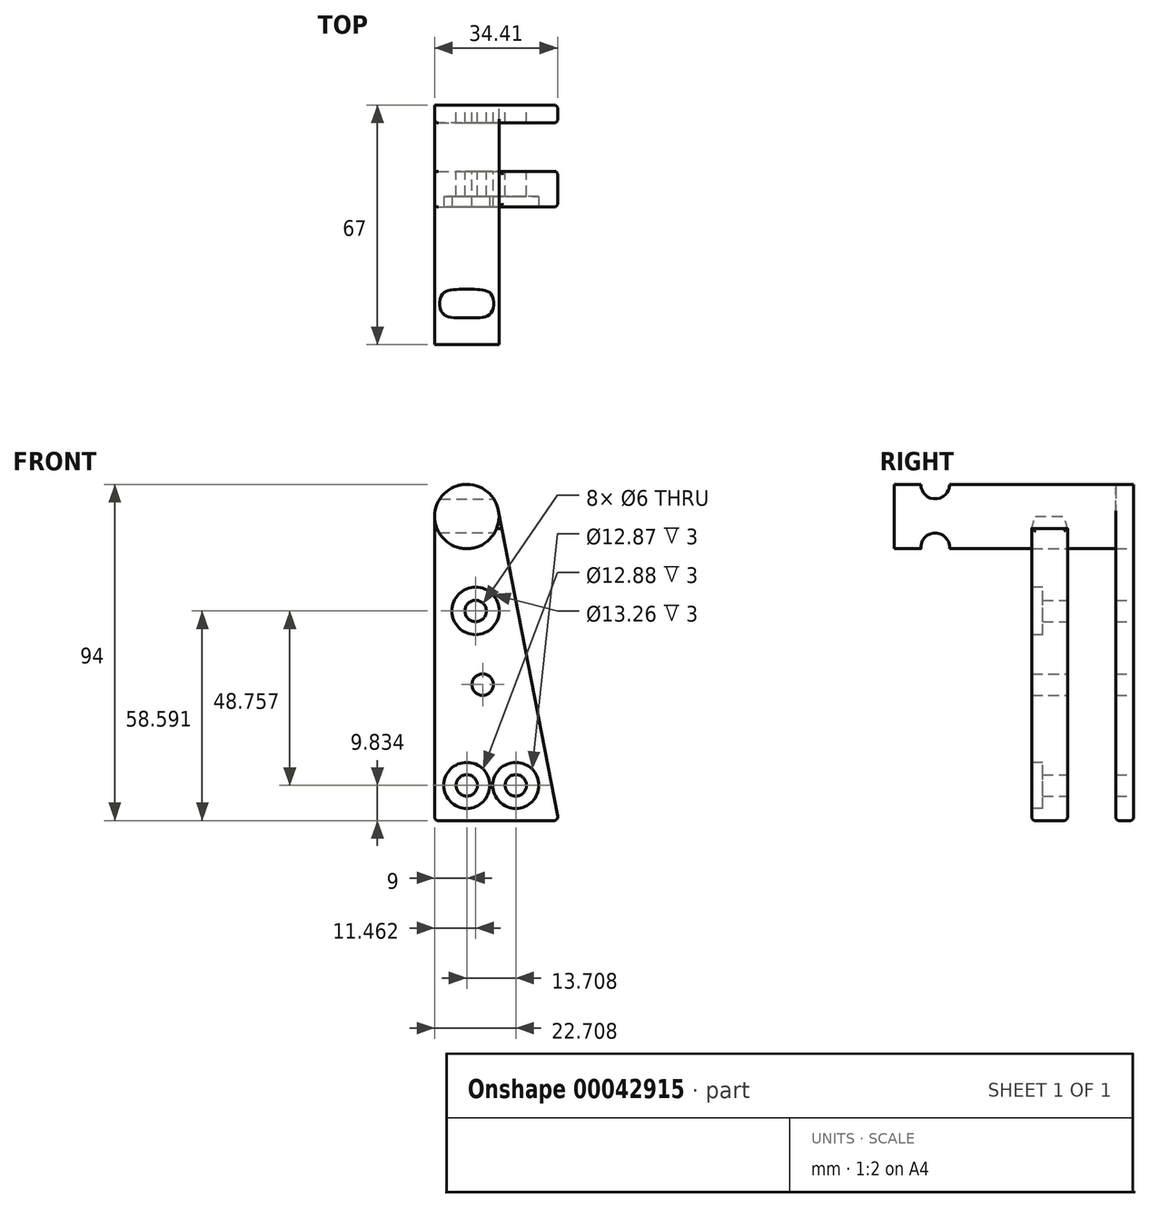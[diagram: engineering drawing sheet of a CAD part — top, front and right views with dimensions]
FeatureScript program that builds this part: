
annotation { "Feature Type Name" : "Feature", "Feature Type Description" : "" }
export const myFeature = defineFeature(function(context is Context, id is Id, definition is map)
    precondition{}
    {
        {
            var Q0;
            Q0=qCreatedBy(makeId("Front.planeOp"),FACE);
            var sketch = newSketch(context, id + "F0", { "sketchPlane" : qUnion([Q0])});
            skCircle(sketch, "E0", {"center": v(0, 0) * mm, "radius": 9 * mm});
            skLineSegment(sketch, "E1", {"start": v(-9, 0) * mm, "end": v(-9, -85) * mm});
            skLineSegment(sketch, "E2", {"start": v(-9, -85) * mm, "end": v(25.62, -85) * mm});
            skLineSegment(sketch, "E3", {"start": v(25.62, -85) * mm, "end": v(8.84, 1.71) * mm});
            skCircle(sketch, "E4", {"center": v(4.44, -47) * mm, "radius": 3 * mm});
            skCircle(sketch, "E5", {"center": v(13.7, -75.17) * mm, "radius": 3 * mm});
            skCircle(sketch, "E6", {"center": v(2.46, -26.4) * mm, "radius": 3 * mm});
            skCircle(sketch, "E7", {"center": v(0, -75.17) * mm, "radius": 3 * mm});
            skCircle(sketch, "E8", {"center": v(2.46, -26.4) * mm, "radius": 6.5 * mm});
            skCircle(sketch, "E9", {"center": v(0, -75.17) * mm, "radius": 6.5 * mm});
            skCircle(sketch, "E10", {"center": v(13.7, -75.17) * mm, "radius": 6.5 * mm});
            skSolve(sketch);
        }
        {
            var Q0;
            {var subQ0=sQuery(id+"F0.wireOp",EDGE,"E0");var subQ1=makeQuery(id+"F0.imprint","INTERSECT",VERTEX,{"derivedFrom":[subQ0,sQuery(id+"F0.wireOp",EDGE,"E1")]});Q0=makeQuery(id+"F0.imprint","IMPRINT",FACE,{"disambiguationData":[TD([[makeQuery(id+"F0.imprint","IMPRINT",EDGE,{"disambiguationData":[TD([[subQ1,1.0]])],"derivedFrom":subQ0}),1.0]])]});}
            extrude(context, id + "F1", {"entities" : qUnion([Q0]), "depth" : 67 * mm});
        }
        {
            var Q0;
            {var subQ1=sQuery(id+"F0.wireOp",EDGE,"E1");Q0=makeQuery(id+"F0.imprint","IMPRINT",FACE,{"disambiguationData":[TD([[makeQuery(id+"F0.imprint","IMPRINT",EDGE,{"derivedFrom":subQ1}),1.0]])]});}
            var Q1;
            Q1=makeQuery(id+"F0.imprint","IMPRINT",FACE,{"disambiguationData":[TD([[makeQuery(id+"F0.imprint","IMPRINT",EDGE,{"derivedFrom":sQuery(id+"F0.wireOp",EDGE,"E7")}),-1.0]])]});
            var Q2;
            Q2=makeQuery(id+"F0.imprint","IMPRINT",FACE,{"disambiguationData":[TD([[makeQuery(id+"F0.imprint","IMPRINT",EDGE,{"derivedFrom":sQuery(id+"F0.wireOp",EDGE,"E5")}),-1.0]])]});
            var Q3;
            Q3=makeQuery(id+"F0.imprint","IMPRINT",FACE,{"disambiguationData":[TD([[makeQuery(id+"F0.imprint","IMPRINT",EDGE,{"derivedFrom":sQuery(id+"F0.wireOp",EDGE,"E6")}),-1.0]])]});
            extrude(context, id + "F2", {"entities" : qUnion([Q0, Q1, Q2, Q3]), "depth" : 28.5 * mm, "hasSecondDirection" : true, "secondDirectionOppositeDirection" : false, "secondDirectionDepth" : 18.5 * mm});
        }
        {
            var Q0;
            Q0=qCreatedBy(makeId("Right.planeOp"),FACE);
            var sketch = newSketch(context, id + "F3", { "sketchPlane" : qUnion([Q0])});
            skCircle(sketch, "E11", {"center": v(-55.5, 8.91) * mm, "radius": 4 * mm});
            skCircle(sketch, "E12", {"center": v(-55.5, -8.58) * mm, "radius": 4 * mm});
            skSolve(sketch);
        }
        {
            var Q0;
            Q0=makeQuery(id+"F3.imprint","IMPRINT",FACE,{"disambiguationData":[TD([[makeQuery(id+"F3.imprint","IMPRINT",EDGE,{"derivedFrom":sQuery(id+"F3.wireOp",EDGE,"E11")}),1.0]])]});
            var Q1;
            Q1=makeQuery(id+"F3.imprint","IMPRINT",FACE,{"disambiguationData":[TD([[makeQuery(id+"F3.imprint","IMPRINT",EDGE,{"derivedFrom":sQuery(id+"F3.wireOp",EDGE,"E12")}),1.0]])]});
            extrude(context, id + "F4", {"entities" : qUnion([Q0, Q1]), "operationType" : NewBodyOperationType.REMOVE, "oppositeDirection" : true, "depth" : 25 * mm, "hasSecondDirection" : true, "secondDirectionOppositeDirection" : false, "secondDirectionDepth" : 51.98 * mm});
        }
        {
            var Q0;
            {var subQ0=sQuery(id+"F0.wireOp",EDGE,"E0");var subQ1=makeQuery(id+"F0.imprint","INTERSECT",VERTEX,{"derivedFrom":[subQ0,sQuery(id+"F0.wireOp",EDGE,"E1")]});Q0=makeQuery(id+"F0.imprint","IMPRINT",FACE,{"disambiguationData":[TD([[makeQuery(id+"F0.imprint","IMPRINT",EDGE,{"disambiguationData":[TD([[subQ1,1.0]])],"derivedFrom":subQ0}),1.0]])]});}
            var Q1;
            {var subQ1=sQuery(id+"F0.wireOp",EDGE,"E1");Q1=makeQuery(id+"F0.imprint","IMPRINT",FACE,{"disambiguationData":[TD([[makeQuery(id+"F0.imprint","IMPRINT",EDGE,{"derivedFrom":subQ1}),1.0]])]});}
            var Q2;
            Q2=makeQuery(id+"F0.imprint","IMPRINT",FACE,{"disambiguationData":[TD([[makeQuery(id+"F0.imprint","IMPRINT",EDGE,{"derivedFrom":sQuery(id+"F0.wireOp",EDGE,"E6")}),-1.0]])]});
            var Q3;
            Q3=makeQuery(id+"F0.imprint","IMPRINT",FACE,{"disambiguationData":[TD([[makeQuery(id+"F0.imprint","IMPRINT",EDGE,{"derivedFrom":sQuery(id+"F0.wireOp",EDGE,"E5")}),-1.0]])]});
            var Q4;
            Q4=makeQuery(id+"F0.imprint","IMPRINT",FACE,{"disambiguationData":[TD([[makeQuery(id+"F0.imprint","IMPRINT",EDGE,{"derivedFrom":sQuery(id+"F0.wireOp",EDGE,"E7")}),-1.0]])]});
            extrude(context, id + "F5", {"entities" : qUnion([Q0, Q1, Q2, Q3, Q4]), "depth" : 5 * mm});
        }
        {
            var Q0;
            Q0=makeQuery(id+"F2.opExtrude","CAP_FACE",FACE,{"disambiguationData":[OSD([sQuery(id+"F0.wireOp",EDGE,"E0"),sQuery(id+"F0.wireOp",EDGE,"E1"),sQuery(id+"F0.wireOp",EDGE,"E2"),sQuery(id+"F0.wireOp",EDGE,"E3"),sQuery(id+"F0.wireOp",EDGE,"E4"),sQuery(id+"F0.wireOp",EDGE,"E5"),sQuery(id+"F0.wireOp",EDGE,"E6"),sQuery(id+"F0.wireOp",EDGE,"E7")])],"isStart":false});
            var sketch = newSketch(context, id + "F6", { "sketchPlane" : qUnion([Q0])});
            skCircle(sketch, "E13", {"center": v(13.7, -75.17) * mm, "radius": 6.44 * mm});
            skCircle(sketch, "E14", {"center": v(0, -75.17) * mm, "radius": 6.44 * mm});
            skCircle(sketch, "E15", {"center": v(2.46, -26.4) * mm, "radius": 6.63 * mm});
            skSolve(sketch);
        }
        {
            var Q0;
            Q0=makeQuery(id+"F6.imprint","IMPRINT",FACE,{"disambiguationData":[TD([[makeQuery(id+"F6.imprint","IMPRINT",EDGE,{"derivedFrom":sQuery(id+"F6.wireOp",EDGE,"E13")}),1.0]])]});
            var Q1;
            Q1=makeQuery(id+"F6.imprint","IMPRINT",FACE,{"disambiguationData":[TD([[makeQuery(id+"F6.imprint","IMPRINT",EDGE,{"derivedFrom":sQuery(id+"F6.wireOp",EDGE,"E14")}),1.0]])]});
            var Q2;
            Q2=makeQuery(id+"F6.imprint","IMPRINT",FACE,{"disambiguationData":[TD([[makeQuery(id+"F6.imprint","IMPRINT",EDGE,{"derivedFrom":sQuery(id+"F6.wireOp",EDGE,"E15")}),1.0]])]});
            extrude(context, id + "F7", {"entities" : qUnion([Q0, Q1, Q2]), "operationType" : NewBodyOperationType.REMOVE, "oppositeDirection" : true, "depth" : 3 * mm});
        }
        {
            var Q0;
            Q0=makeQuery(id+"F2.opExtrude","CAP_EDGE",EDGE,{"disambiguationData":[OSD([sQuery(id+"F0.wireOp",EDGE,"E1")])],"isStart":false});
            var Q1;
            Q1=makeQuery(id+"F2.opExtrude","CAP_EDGE",EDGE,{"disambiguationData":[OSD([sQuery(id+"F0.wireOp",EDGE,"E1")])],"isStart":true});
            var Q2;
            Q2=makeQuery(id+"F2.opExtrude","SWEPT_EDGE",EDGE,{"disambiguationData":[OSD([sQuery(id+"F0.wireOp",EDGE,"E1"),sQuery(id+"F0.wireOp",EDGE,"E2")])]});
            var Q3;
            Q3=makeQuery(id+"F5.opExtrude","CAP_EDGE",EDGE,{"disambiguationData":[OSD([sQuery(id+"F0.wireOp",EDGE,"E1")])],"isStart":true});
            var Q4;
            Q4=makeQuery(id+"F5.opExtrude","CAP_EDGE",EDGE,{"disambiguationData":[OSD([sQuery(id+"F0.wireOp",EDGE,"E1")])],"isStart":false});
            var Q5;
            Q5=makeQuery(id+"F2.opExtrude","SWEPT_FACE",FACE,{"disambiguationData":[OSD([sQuery(id+"F0.wireOp",EDGE,"E2")])]});
            var Q6;
            Q6=makeQuery(id+"F5.opExtrude","SWEPT_FACE",FACE,{"disambiguationData":[OSD([sQuery(id+"F0.wireOp",EDGE,"E2")])]});
            var Q7;
            Q7=makeQuery(id+"F2.opExtrude","CAP_EDGE",EDGE,{"disambiguationData":[OSD([sQuery(id+"F0.wireOp",EDGE,"E3")])],"isStart":false});
            var Q8;
            Q8=makeQuery(id+"F2.opExtrude","SWEPT_FACE",FACE,{"disambiguationData":[OSD([sQuery(id+"F0.wireOp",EDGE,"E3")])]});
            fillet(context, id + "F8", {"entities" : qUnion([Q0, Q1, Q2, Q3, Q4, Q5, Q6, Q7, Q8]), "radius" : 1 * mm, "tangentPropagation" : true, "allowEdgeOverflow" : false});
        }
    });
